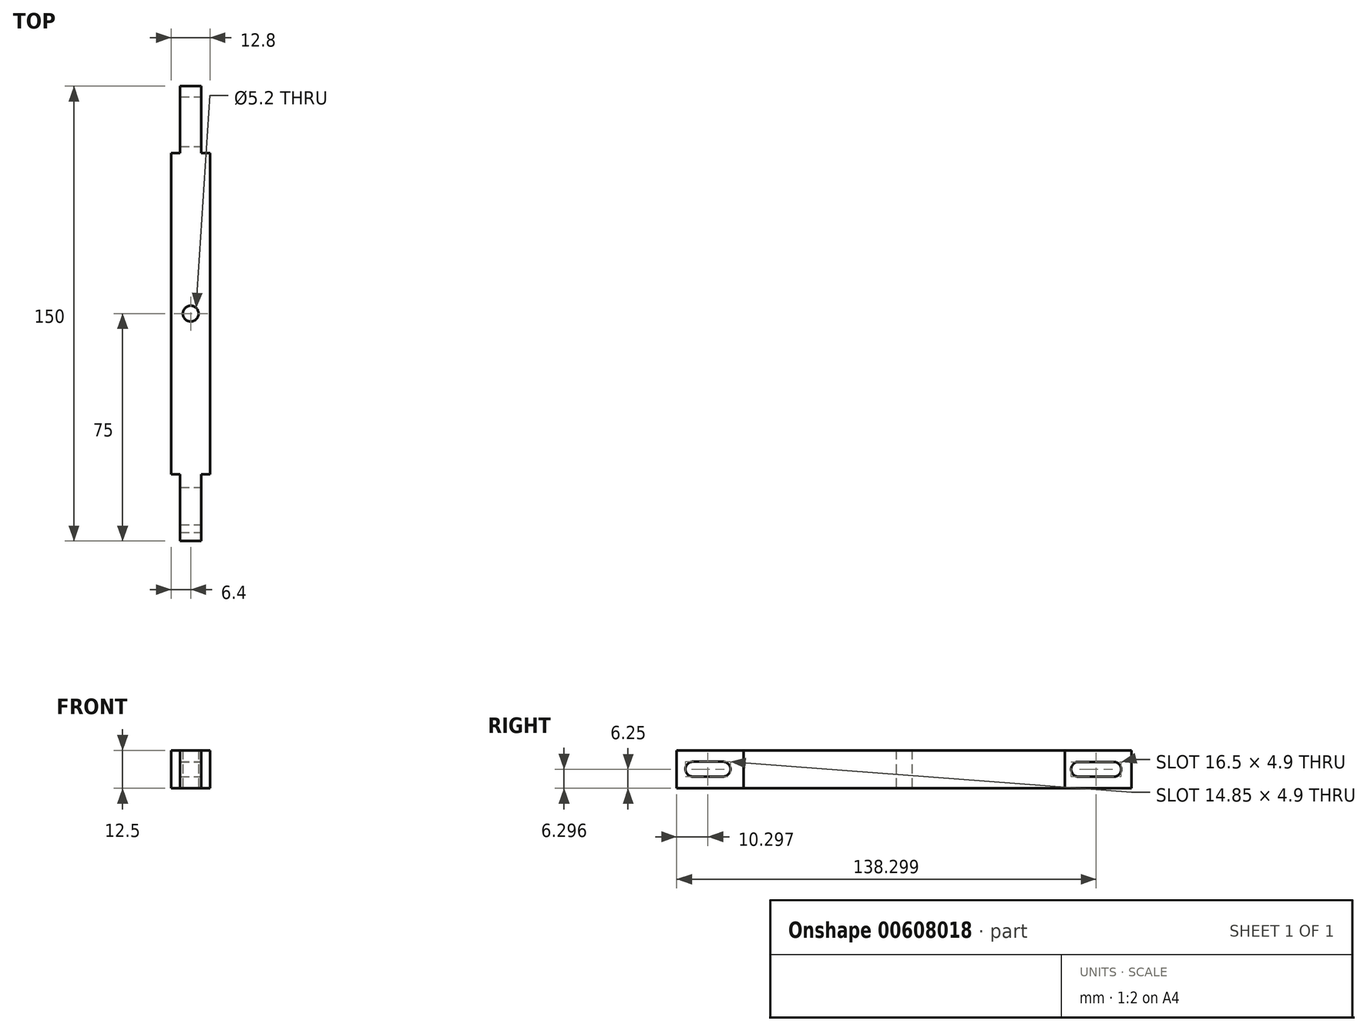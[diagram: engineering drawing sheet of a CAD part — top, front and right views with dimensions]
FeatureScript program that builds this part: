
annotation { "Feature Type Name" : "Feature", "Feature Type Description" : "" }
export const myFeature = defineFeature(function(context is Context, id is Id, definition is map)
    precondition{}
    {
        {
            var Q0;
            Q0=qCreatedBy(makeId("Top.planeOp"),FACE);
            var sketch = newSketch(context, id + "F0", { "sketchPlane" : qUnion([Q0])});
            skCircle(sketch, "E0", {"center": v(0, 0) * mm, "radius": 2.6 * mm});
            skLineSegment(sketch, "E1.bottom", {"start": v(6.4, -53) * mm, "end": v(3.5, -53) * mm});
            skLineSegment(sketch, "E1.top", {"start": v(6.4, 53) * mm, "end": v(3.5, 53) * mm});
            skLineSegment(sketch, "E1.left", {"start": v(6.4, -53) * mm, "end": v(6.4, 53) * mm});
            skLineSegment(sketch, "E1.right", {"start": v(-6.4, -53) * mm, "end": v(-6.4, 53) * mm});
            skLineSegment(sketch, "E2.bottom", {"start": v(3.5, -75) * mm, "end": v(-3.5, -75) * mm});
            skLineSegment(sketch, "E2.left", {"start": v(3.5, -75) * mm, "end": v(3.5, -53) * mm});
            skLineSegment(sketch, "E2.right", {"start": v(-3.5, -75) * mm, "end": v(-3.5, -53) * mm});
            skPoint(sketch, "E2.middle", {"position": v(0, -53) * mm});
            skLineSegment(sketch, "E3.MirrorCS", {"start": v(3.5, 75) * mm, "end": v(3.5, 53) * mm});
            skLineSegment(sketch, "E4.MirrorCS", {"start": v(-3.5, 75) * mm, "end": v(-3.5, 53) * mm});
            skLineSegment(sketch, "E5.MirrorCS", {"start": v(3.5, 75) * mm, "end": v(-3.5, 75) * mm});
            skLineSegment(sketch, "E6.trimOffspring", {"start": v(-3.5, 53) * mm, "end": v(-6.4, 53) * mm});
            skPoint(sketch, "E7.MirrorCS.end.orphan", {"position": v(-3.5, 31) * mm});
            skPoint(sketch, "E7.MirrorCS.start.orphan", {"position": v(3.5, 31) * mm});
            skPoint(sketch, "E2.top.start.orphan", {"position": v(3.5, -31) * mm});
            skPoint(sketch, "E8.orphan", {"position": v(-3.5, -31) * mm});
            skLineSegment(sketch, "E9.trimOffspring", {"start": v(-3.5, -53) * mm, "end": v(-6.4, -53) * mm});
            skSolve(sketch);
        }
        {
            var Q0;
            Q0 = qSketchRegion(id + "F0", true);
            extrude(context, id + "F1", {"entities" : qUnion([Q0]), "depth" : 12.5 * mm, "offsetDistance" : 25 * mm});
        }
        {
            var Q0;
            Q0=makeQuery(id+"F1.opExtrude","SWEPT_FACE",FACE,{"disambiguationData":[OSD([sQuery(id+"F0.wireOp",EDGE,"E3.MirrorCS")])]});
            var sketch = newSketch(context, id + "F2", { "sketchPlane" : qUnion([Q0])});
            skLineSegment(sketch, "E10", {"start": v(75, 6.25) * mm, "end": v(75, 6.25) * mm});
            skPoint(sketch, "E10.endSnap0", {"position": v(53, 6.25) * mm});
            skArc(sketch, "E11", {"start": v(57.5, 8.7) * mm, "mid": v(55.05, 6.25) * mm, "end": v(57.5, 3.8) * mm});
            skArc(sketch, "E12", {"start": v(69.1, 3.8) * mm, "mid": v(71.55, 6.25) * mm, "end": v(69.1, 8.7) * mm});
            skLineSegment(sketch, "E13", {"start": v(69.1, 8.7) * mm, "end": v(57.5, 8.7) * mm});
            skLineSegment(sketch, "E14", {"start": v(69.1, 3.8) * mm, "end": v(57.5, 3.8) * mm});
            skSolve(sketch);
        }
        {
            var Q0;
            Q0 = qSketchRegion(id + "F2", true);
            extrude(context, id + "F3", {"entities" : qUnion([Q0]), "operationType" : NewBodyOperationType.REMOVE, "oppositeDirection" : true, "depth" : 25 * mm, "offsetDistance" : 25 * mm});
        }
        {
            var Q0;
            Q0=makeQuery(id+"F1.opExtrude","SWEPT_FACE",FACE,{"disambiguationData":[OSD([sQuery(id+"F0.wireOp",EDGE,"E2.left")])]});
            var sketch = newSketch(context, id + "F4", { "sketchPlane" : qUnion([Q0])});
            skSolve(sketch);
        }
        {
            var Q0;
            {var subQ0=sQuery(id+"F0.wireOp",EDGE,"E2.left");Q0=makeQuery(id+"F4.imprint","IMPRINT",FACE,{"disambiguationData":[TD([[makeQuery(id+"F4.imprint","IMPRINT",EDGE,{"derivedFrom":makeQuery(id+"F1.opExtrude","CAP_EDGE",EDGE,{"disambiguationData":[OSD([subQ0])],"isStart":true})}),1.0]])]});}
            var sketch = newSketch(context, id + "F5", { "sketchPlane" : qUnion([Q0])});
            skArc(sketch, "E15", {"start": v(-69.65, 8.75) * mm, "mid": v(-72.13, 6.31) * mm, "end": v(-69.68, 3.85) * mm});
            skArc(sketch, "E16", {"start": v(-59.73, 3.85) * mm, "mid": v(-57.28, 6.3) * mm, "end": v(-59.73, 8.75) * mm});
            skLineSegment(sketch, "E17", {"start": v(-69.71, 8.75) * mm, "end": v(-59.73, 8.75) * mm});
            skLineSegment(sketch, "E18", {"start": v(-69.68, 3.85) * mm, "end": v(-59.73, 3.85) * mm});
            skSolve(sketch);
        }
        {
            var Q0;
            Q0 = qSketchRegion(id + "F5", true);
            extrude(context, id + "F6", {"entities" : qUnion([Q0]), "operationType" : NewBodyOperationType.REMOVE, "oppositeDirection" : true, "depth" : 25 * mm, "offsetDistance" : 25 * mm});
        }
    });
